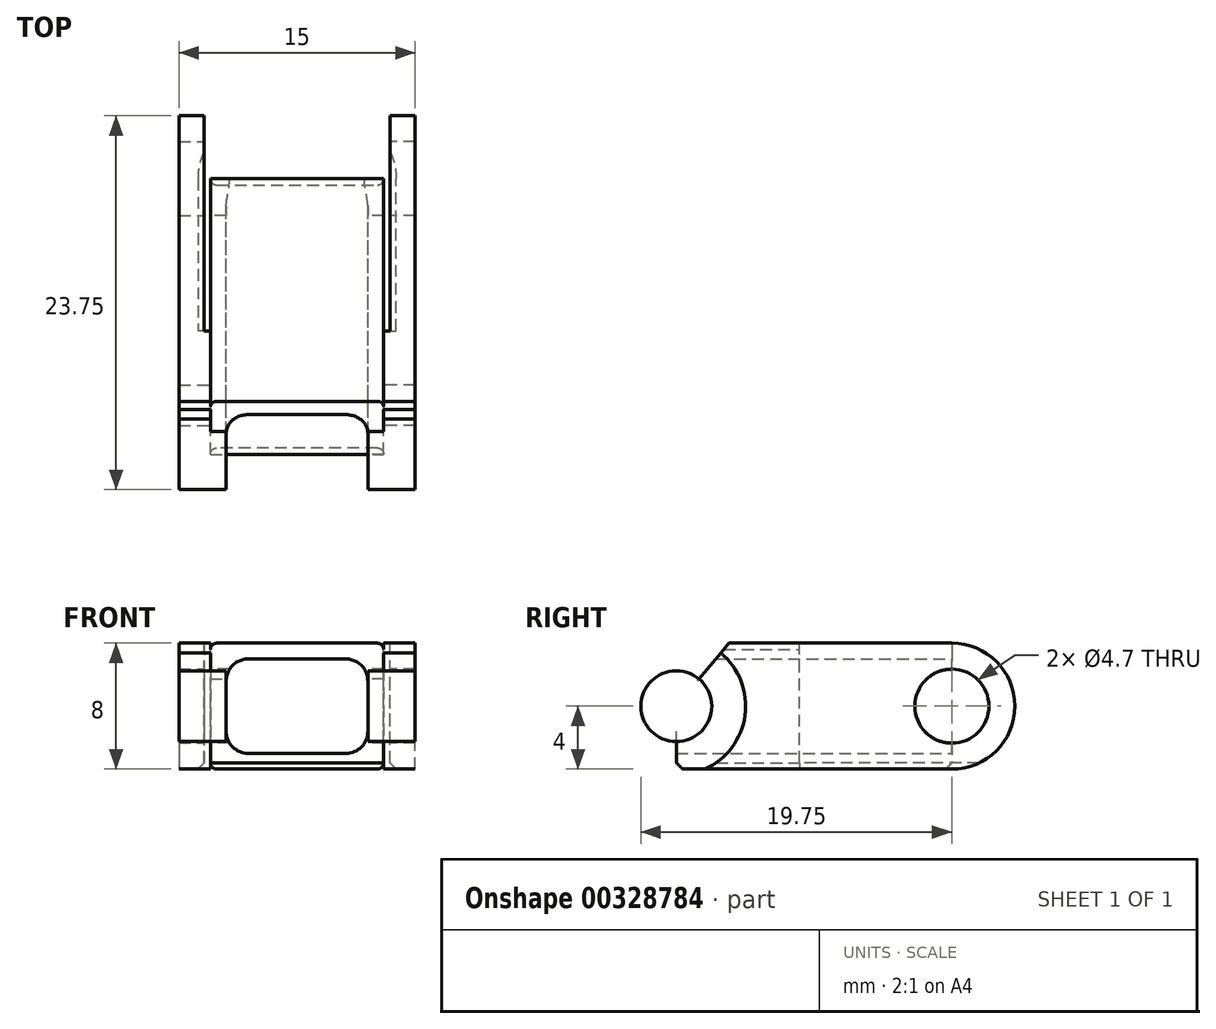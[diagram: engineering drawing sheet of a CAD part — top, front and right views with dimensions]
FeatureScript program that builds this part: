
annotation { "Feature Type Name" : "Feature", "Feature Type Description" : "" }
export const myFeature = defineFeature(function(context is Context, id is Id, definition is map)
    precondition{}
    {
        {
            var Q0;
            Q0=qCreatedBy(makeId("Front.planeOp"),FACE);
            var sketch = newSketch(context, id + "F0", { "sketchPlane" : qUnion([Q0])});
            skLineSegment(sketch, "E0.bottom", {"start": v(3.1, -3) * mm, "end": v(-3.1, -3) * mm});
            skLineSegment(sketch, "E0.top", {"start": v(3.1, 3) * mm, "end": v(-3.1, 3) * mm});
            skLineSegment(sketch, "E0.left", {"start": v(4.5, -1.6) * mm, "end": v(4.5, 1.6) * mm});
            skLineSegment(sketch, "E0.right", {"start": v(-4.5, -1.6) * mm, "end": v(-4.5, 1.6) * mm});
            skPoint(sketch, "E0.middle", {"position": v(0, 0) * mm});
            skPoint(sketch, "E1.visualSharp", {"position": v(-4.5, 3) * mm});
            skArc(sketch, "E1.filletArc", {"start": v(-3.1, 3) * mm, "mid": v(-4.09, 2.59) * mm, "end": v(-4.5, 1.6) * mm});
            skPoint(sketch, "E2.visualSharp", {"position": v(4.5, 3) * mm});
            skArc(sketch, "E2.filletArc", {"start": v(4.5, 1.6) * mm, "mid": v(4.09, 2.59) * mm, "end": v(3.1, 3) * mm});
            skPoint(sketch, "E3.visualSharp", {"position": v(4.5, -3) * mm});
            skArc(sketch, "E3.filletArc", {"start": v(3.1, -3) * mm, "mid": v(4.09, -2.59) * mm, "end": v(4.5, -1.6) * mm});
            skPoint(sketch, "E4.visualSharp", {"position": v(-4.5, -3) * mm});
            skArc(sketch, "E4.filletArc", {"start": v(-4.5, -1.6) * mm, "mid": v(-4.09, -2.59) * mm, "end": v(-3.1, -3) * mm});
            skLineSegment(sketch, "E5.bottom", {"start": v(-5.1, 4) * mm, "end": v(5.1, 4) * mm});
            skLineSegment(sketch, "E5.top", {"start": v(-5.1, -4) * mm, "end": v(5.1, -4) * mm});
            skLineSegment(sketch, "E5.left", {"start": v(-5.5, 3.6) * mm, "end": v(-5.5, -3.6) * mm});
            skLineSegment(sketch, "E5.right", {"start": v(5.5, 3.6) * mm, "end": v(5.5, -3.6) * mm});
            skPoint(sketch, "E6.visualSharp", {"position": v(-5.5, 4) * mm});
            skArc(sketch, "E6.filletArc", {"start": v(-5.1, 4) * mm, "mid": v(-5.38, 3.88) * mm, "end": v(-5.5, 3.6) * mm});
            skPoint(sketch, "E7.visualSharp", {"position": v(5.5, 4) * mm});
            skArc(sketch, "E7.filletArc", {"start": v(5.5, 3.6) * mm, "mid": v(5.38, 3.88) * mm, "end": v(5.1, 4) * mm});
            skPoint(sketch, "E8.visualSharp", {"position": v(5.5, -4) * mm});
            skArc(sketch, "E8.filletArc", {"start": v(5.1, -4) * mm, "mid": v(5.38, -3.88) * mm, "end": v(5.5, -3.6) * mm});
            skPoint(sketch, "E9.visualSharp", {"position": v(-5.5, -4) * mm});
            skArc(sketch, "E9.filletArc", {"start": v(-5.5, -3.6) * mm, "mid": v(-5.38, -3.88) * mm, "end": v(-5.1, -4) * mm});
            skSolve(sketch);
        }
        {
            var Q0;
            Q0=qSketchRegion(id+"F0",true);
            extrude(context, id + "F1", {"entities" : qUnion([Q0]), "depth" : 17.5 * mm});
        }
        {
            var Q0;
            Q0=makeQuery(id+"F1.opExtrude","SWEPT_FACE",FACE,{"disambiguationData":[OSD([sQuery(id+"F0.wireOp",EDGE,"E5.right")])]});
            var sketch = newSketch(context, id + "F2", { "sketchPlane" : qUnion([Q0])});
            skLineSegment(sketch, "E10", {"start": v(-17.5, 0) * mm, "end": v(-14.14, 4) * mm});
            skLineSegment(sketch, "E11", {"start": v(-17.5, 0) * mm, "end": v(-17.5, 4) * mm});
            skLineSegment(sketch, "E12", {"start": v(-17.5, 4) * mm, "end": v(-14.14, 4) * mm});
            skSolve(sketch);
        }
        {
            var Q0;
            {var subQ0=sQuery(id+"F2.wireOp",EDGE,"E11");var subQ1=sQuery(id+"F2.wireOp",EDGE,"E10");var subQ2=sQuery(id+"F0.wireOp",EDGE,"E5.right");var subQ3=makeQuery(id+"F2.imprint","INTERSECT",VERTEX,{"derivedFrom":[makeQuery(id+"F1.opExtrude","CAP_EDGE",EDGE,{"disambiguationData":[OSD([subQ2])],"isStart":false}),subQ1,subQ0]});Q0=makeQuery(id+"F2.imprint","IMPRINT",FACE,{"disambiguationData":[TD([[makeQuery(id+"F2.imprint","IMPRINT",EDGE,{"disambiguationData":[TD([[subQ3,-1.0]])],"derivedFrom":subQ1}),1.0]])]});}
            var Q1;
            {var subQ0=sQuery(id+"F2.wireOp",EDGE,"E12");Q1=makeQuery(id+"F2.imprint","IMPRINT",FACE,{"disambiguationData":[TD([[makeQuery(id+"F2.imprint","IMPRINT",EDGE,{"derivedFrom":subQ0}),-1.0]])]});}
            var Q2;
            Q2=sQuery(id+"F2.wireOp",EDGE,"d9586431-e679-4d5a-a5e5-9d37ee124d94.0");
            var Q3;
            Q3=makeQuery(id+"F1.opExtrude","SWEPT_FACE",FACE,{"disambiguationData":[OSD([sQuery(id+"F0.wireOp",EDGE,"E5.left")])]});
            extrude(context, id + "F3", {"entities" : qUnion([Q0, Q1]), "operationType" : NewBodyOperationType.REMOVE, "surfaceEntities" : qUnion([Q2]), "endBound" : BoundingType.UP_TO_SURFACE, "oppositeDirection" : true, "endBoundEntityFace" : qUnion([Q3]), "depth" : 12 * mm});
        }
        {
            var Q0;
            Q0=makeQuery(id+"F1.opExtrude","SWEPT_FACE",FACE,{"disambiguationData":[OSD([sQuery(id+"F0.wireOp",EDGE,"E5.right")])]});
            var sketch = newSketch(context, id + "F4", { "sketchPlane" : qUnion([Q0])});
            skCircle(sketch, "E13", {"center": v(-17.5, 0) * mm, "radius": 2.25 * mm});
            skSolve(sketch);
        }
        {
            var Q0;
            Q0=qSketchRegion(id+"F4",true);
            extrude(context, id + "F5", {"entities" : qUnion([Q0]), "operationType" : NewBodyOperationType.ADD, "depth" : 2 * mm, "hasSecondDirection" : true, "secondDirectionOppositeDirection" : true, "secondDirectionDepth" : 1 * mm});
        }
        {
            var Q0;
            Q0=makeQuery(id+"F1.opExtrude","SWEPT_FACE",FACE,{"disambiguationData":[OSD([sQuery(id+"F0.wireOp",EDGE,"E5.left")])]});
            var sketch = newSketch(context, id + "F6", { "sketchPlane" : qUnion([Q0])});
            skArc(sketch, "E14.0", {"start": v(16.05, 1.72) * mm, "mid": v(19.61, 0.77) * mm, "end": v(17.5, -2.25) * mm, "construction": true});
            skCircle(sketch, "E15", {"center": v(17.5, 0) * mm, "radius": 2.25 * mm});
            skSolve(sketch);
        }
        {
            var Q0;
            {var subQ0=sQuery(id+"F6.wireOp",EDGE,"E15");var subQ1=sQuery(id+"F0.wireOp",EDGE,"E5.left");var subQ2=makeQuery(id+"F1.opExtrude","CAP_EDGE",EDGE,{"disambiguationData":[OSD([subQ1])],"isStart":false});var subQ3=makeQuery(id+"F6.imprint","INTERSECT",VERTEX,{"derivedFrom":[subQ2,subQ0]});Q0=makeQuery(id+"F6.imprint","IMPRINT",FACE,{"disambiguationData":[TD([[makeQuery(id+"F6.imprint","IMPRINT",EDGE,{"disambiguationData":[TD([[subQ3,-1.0]])],"derivedFrom":subQ0}),1.0]])]});}
            var Q1;
            {var subQ0=sQuery(id+"F6.wireOp",EDGE,"E15");var subQ1=sQuery(id+"F0.wireOp",EDGE,"E5.left");var subQ2=makeQuery(id+"F1.opExtrude","CAP_EDGE",EDGE,{"disambiguationData":[OSD([subQ1])],"isStart":false});var subQ3=makeQuery(id+"F6.imprint","INTERSECT",VERTEX,{"derivedFrom":[subQ2,subQ0]});Q1=makeQuery(id+"F6.imprint","IMPRINT",FACE,{"disambiguationData":[TD([[makeQuery(id+"F6.imprint","IMPRINT",EDGE,{"disambiguationData":[TD([[subQ3,1.0]])],"derivedFrom":subQ0}),1.0]])]});}
            extrude(context, id + "F7", {"entities" : qUnion([Q0, Q1]), "operationType" : NewBodyOperationType.ADD, "depth" : 2 * mm, "hasSecondDirection" : true, "secondDirectionOppositeDirection" : true, "secondDirectionDepth" : 1 * mm});
        }
        {
            var Q0;
            Q0=makeQuery(id+"F1.opExtrude","SWEPT_FACE",FACE,{"disambiguationData":[OSD([sQuery(id+"F0.wireOp",EDGE,"E5.right")])]});
            cPlane(context, id + "F8", {"entities" : qUnion([Q0]), "cplaneType" : CPlaneType.OFFSET, "offset" : 0.4 * mm, "width" : 150 * mm, "height" : 150 * mm});
        }
        {
            var Q0;
            Q0=qCreatedBy(id+"F8.planeOp",FACE);
            var sketch = newSketch(context, id + "F9", { "sketchPlane" : qUnion([Q0])});
            skCircle(sketch, "E16", {"center": v(0, 0) * mm, "radius": 2.35 * mm});
            skArc(sketch, "E17", {"start": v(0, 4) * mm, "mid": v(4, 0) * mm, "end": v(0, -4) * mm});
            skCircle(sketch, "E18.0", {"center": v(-17.5, 0) * mm, "radius": 2.25 * mm, "construction": true});
            skArc(sketch, "E19", {"start": v(-15.67, 4) * mm, "mid": v(-13.1, 0) * mm, "end": v(-15.67, -4) * mm});
            skLineSegment(sketch, "E20", {"start": v(0, 4) * mm, "end": v(-15.67, 4) * mm});
            skLineSegment(sketch, "E21", {"start": v(0, -4) * mm, "end": v(-15.67, -4) * mm});
            skSolve(sketch);
        }
        {
            var Q0;
            Q0=qSketchRegion(id+"F9",true);
            extrude(context, id + "F10", {"entities" : qUnion([Q0]), "depth" : 1.6 * mm});
        }
        {
            var Q0;
            Q0=makeQuery(id+"F10.opExtrude","CAP_FACE",FACE,{"disambiguationData":[OSD([sQuery(id+"F9.wireOp",EDGE,"E16"),sQuery(id+"F9.wireOp",EDGE,"E17"),sQuery(id+"F9.wireOp",EDGE,"E19"),sQuery(id+"F9.wireOp",EDGE,"E20"),sQuery(id+"F9.wireOp",EDGE,"E21")])],"isStart":true});
            var sketch = newSketch(context, id + "F11", { "sketchPlane" : qUnion([Q0])});
            skArc(sketch, "E22.0", {"start": v(15.67, 4) * mm, "mid": v(13.1, 0) * mm, "end": v(15.67, -4) * mm});
            skLineSegment(sketch, "E23", {"start": v(15.67, -4) * mm, "end": v(9.67, -4) * mm});
            skLineSegment(sketch, "E24", {"start": v(9.67, -4) * mm, "end": v(9.67, 4) * mm});
            skLineSegment(sketch, "E25", {"start": v(9.67, 4) * mm, "end": v(15.67, 4) * mm});
            skSolve(sketch);
        }
        {
            var Q0;
            Q0=qSketchRegion(id+"F11",true);
            extrude(context, id + "F12", {"entities" : qUnion([Q0]), "operationType" : NewBodyOperationType.ADD, "depth" : 0.4 * mm});
        }
        {
            var Q0;
            Q0=makeQuery(id+"F1.opExtrude","SWEPT_FACE",FACE,{"disambiguationData":[OSD([sQuery(id+"F0.wireOp",EDGE,"E5.left")])]});
            cPlane(context, id + "F13", {"entities" : qUnion([Q0]), "cplaneType" : CPlaneType.OFFSET, "offset" : 0.4 * mm, "width" : 150 * mm, "height" : 150 * mm});
        }
        {
            var Q0;
            Q0=qCreatedBy(id+"F13.planeOp",FACE);
            var sketch = newSketch(context, id + "F14", { "sketchPlane" : qUnion([Q0])});
            skArc(sketch, "E26.0", {"start": v(0, 4) * mm, "mid": v(-4, 0) * mm, "end": v(0, -4) * mm});
            skLineSegment(sketch, "E27.0", {"start": v(0, -4) * mm, "end": v(15.67, -4) * mm});
            skLineSegment(sketch, "E28.0", {"start": v(0, 4) * mm, "end": v(15.67, 4) * mm});
            skArc(sketch, "E29.0", {"start": v(15.67, 4) * mm, "mid": v(13.1, 0) * mm, "end": v(15.67, -4) * mm});
            skCircle(sketch, "E30.0", {"center": v(0, 0) * mm, "radius": 2.35 * mm});
            skSolve(sketch);
        }
        {
            var Q0;
            Q0=qSketchRegion(id+"F14",true);
            extrude(context, id + "F15", {"entities" : qUnion([Q0]), "depth" : 1.6 * mm});
        }
        {
            var Q0;
            Q0=makeQuery(id+"F15.opExtrude","CAP_FACE",FACE,{"disambiguationData":[OSD([sQuery(id+"F14.wireOp",EDGE,"E26.0"),sQuery(id+"F14.wireOp",EDGE,"E27.0"),sQuery(id+"F14.wireOp",EDGE,"E28.0"),sQuery(id+"F14.wireOp",EDGE,"E29.0"),sQuery(id+"F14.wireOp",EDGE,"E30.0")])],"isStart":true});
            var sketch = newSketch(context, id + "F16", { "sketchPlane" : qUnion([Q0])});
            skArc(sketch, "E31.0", {"start": v(-15.67, 4) * mm, "mid": v(-13.1, 0) * mm, "end": v(-15.67, -4) * mm});
            skLineSegment(sketch, "E32", {"start": v(-15.67, -4) * mm, "end": v(-9.67, -4) * mm});
            skLineSegment(sketch, "E33", {"start": v(-9.67, -4) * mm, "end": v(-9.67, 4) * mm});
            skLineSegment(sketch, "E34", {"start": v(-9.67, 4) * mm, "end": v(-15.67, 4) * mm});
            skSolve(sketch);
        }
        {
            var Q0;
            Q0=qSketchRegion(id+"F16",true);
            extrude(context, id + "F17", {"entities" : qUnion([Q0]), "operationType" : NewBodyOperationType.ADD, "depth" : 0.4 * mm});
        }
        {
            var Q0;
            {var subQ0=sQuery(id+"F16.wireOp",EDGE,"E33");var subQ3=sQuery(id+"F0.wireOp",EDGE,"E5.left");Q0=makeQuery(id+"F17.boolean.opBoolean","SPLIT",FACE,{"disambiguationData":[TD([makeQuery(id+"F17.opExtrude","SWEPT_FACE",FACE,{"disambiguationData":[OSD([subQ0])]})])],"derivedFrom":makeQuery(id+"F1.opExtrude","SWEPT_FACE",FACE,{"disambiguationData":[OSD([subQ3])]})});}
            var sketch = newSketch(context, id + "F18", { "sketchPlane" : qUnion([Q0])});
            skCircle(sketch, "E35.0", {"center": v(0, 0) * mm, "radius": 2.35 * mm});
            skSolve(sketch);
        }
        {
            var Q0;
            Q0=qSketchRegion(id+"F18",true);
            extrude(context, id + "F19", {"entities" : qUnion([Q0]), "operationType" : NewBodyOperationType.REMOVE, "endBound" : BoundingType.THROUGH_ALL, "oppositeDirection" : true, "depth" : 25 * mm});
        }
        {
            var Q0;
            Q0=makeQuery(id+"F10.opExtrude","CAP_FACE",FACE,{"disambiguationData":[OSD([sQuery(id+"F9.wireOp",EDGE,"E16"),sQuery(id+"F9.wireOp",EDGE,"E17"),sQuery(id+"F9.wireOp",EDGE,"E19"),sQuery(id+"F9.wireOp",EDGE,"E20"),sQuery(id+"F9.wireOp",EDGE,"E21")])],"isStart":false});
            var sketch = newSketch(context, id + "F20", { "sketchPlane" : qUnion([Q0])});
            skPoint(sketch, "E36.0", {"position": v(-15.67, 4) * mm});
            skLineSegment(sketch, "E37.0", {"start": v(-16.05, 1.72) * mm, "end": v(-14.67, 3.37) * mm, "construction": true});
            skArc(sketch, "E38.0", {"start": v(-15.67, 4) * mm, "mid": v(-13.1, 0) * mm, "end": v(-15.67, -4) * mm, "construction": true});
            skLineSegment(sketch, "E39", {"start": v(-14.67, 3.37) * mm, "end": v(-14.14, 4) * mm});
            skLineSegment(sketch, "E40", {"start": v(-15.67, 4) * mm, "end": v(-14.14, 4) * mm});
            skArc(sketch, "E41", {"start": v(-15.67, 4) * mm, "mid": v(-15.15, 3.72) * mm, "end": v(-14.67, 3.37) * mm});
            skSolve(sketch);
        }
        {
            var Q0;
            Q0=qSketchRegion(id+"F20",true);
            var Q1;
            Q1=makeQuery(id+"F15.opExtrude","CAP_FACE",FACE,{"disambiguationData":[OSD([sQuery(id+"F14.wireOp",EDGE,"E26.0"),sQuery(id+"F14.wireOp",EDGE,"E27.0"),sQuery(id+"F14.wireOp",EDGE,"E28.0"),sQuery(id+"F14.wireOp",EDGE,"E29.0"),sQuery(id+"F14.wireOp",EDGE,"E30.0")])],"isStart":false});
            extrude(context, id + "F21", {"entities" : qUnion([Q0]), "operationType" : NewBodyOperationType.REMOVE, "endBound" : BoundingType.UP_TO_SURFACE, "oppositeDirection" : true, "endBoundEntityFace" : qUnion([Q1]), "depth" : 25 * mm});
        }
        {
            var Q0;
            Q0=makeQuery(id+"F1.opExtrude","CAP_EDGE",EDGE,{"disambiguationData":[OSD([sQuery(id+"F0.wireOp",EDGE,"E5.top")])],"isStart":false});
            var Q1;
            Q1=makeQuery(id+"F10.opExtrude","CAP_EDGE",EDGE,{"disambiguationData":[OSD([sQuery(id+"F9.wireOp",EDGE,"E21")])],"isStart":true});
            var Q2;
            Q2=makeQuery(id+"F15.opExtrude","CAP_EDGE",EDGE,{"disambiguationData":[OSD([sQuery(id+"F14.wireOp",EDGE,"E27.0")])],"isStart":true});
            var Q3;
            Q3=makeQuery(id+"F1.opExtrude","CAP_EDGE",EDGE,{"disambiguationData":[OSD([sQuery(id+"F0.wireOp",EDGE,"E5.top")])],"isStart":true});
            chamfer(context, id + "F22", {"entities" : qUnion([Q0, Q1, Q2, Q3]), "width" : 0.4 * mm});
        }
    });
